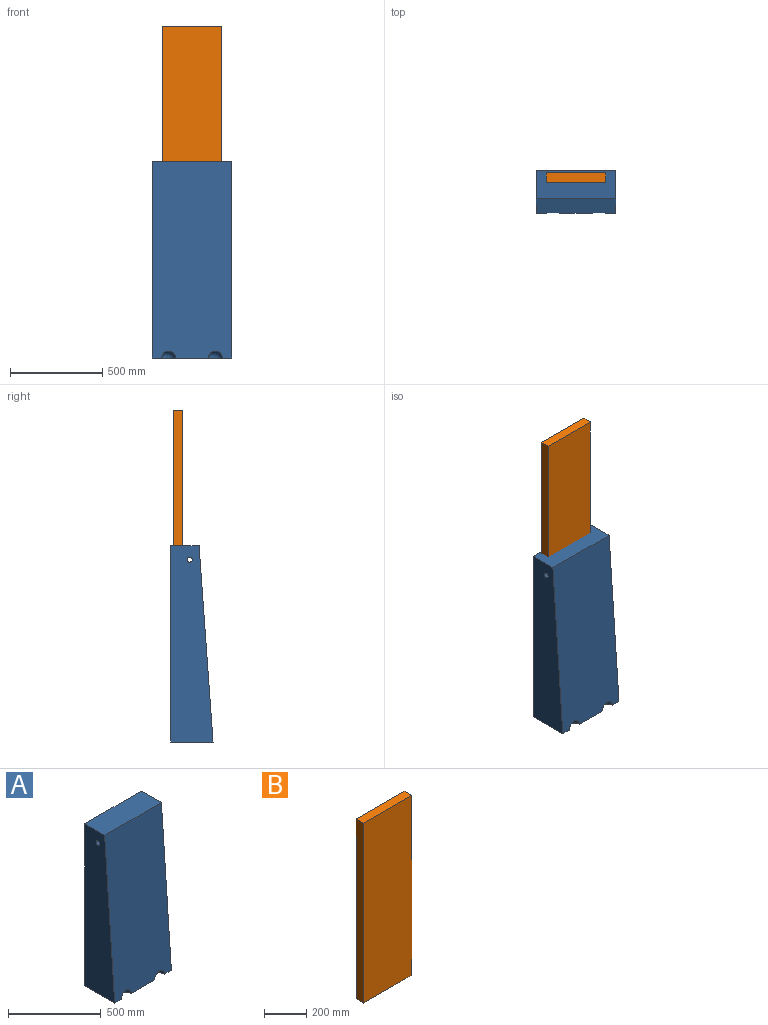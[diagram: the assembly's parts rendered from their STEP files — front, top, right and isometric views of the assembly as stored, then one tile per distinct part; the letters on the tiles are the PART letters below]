
ASSEMBLY  parts=2 mates=1
PART A: 21 faces, bbox 431.8x228.6x1066.8 mm
  f0: plane 431.8x228.6mm, normal (0,0,-1), area 93959.1mm2, adj f1,f3,f4,f5,f6,f7,f8,f10
  f1: plane 1066.8x431.8mm, normal (0,1,0), area 460644.2mm2, adj f0,f2,f4,f5
  f2: plane 431.8x152.4mm, normal (0,0,1), area 65806.3mm2, adj f1,f3,f4,f5
  f3: plane 1066.8x431.8mm, normal (0,-1,0.07), area 457257.5mm2, adj f0,f2,f4,f5,f6,f7
  f4: plane 1066.8x228.6mm, normal (1,0,0), area 202584.1mm2, adj f0,f1,f2,f3,f20
  f5: plane 1066.8x228.6mm, normal (-1,0,0), area 202584.1mm2, adj f0,f1,f2,f3,f20
  f6: sphere r=38.1mm, area 4353.3mm2, adj f0,f3
  f7: sphere r=38.1mm, area 4353.3mm2, adj f0,f3
  f8: cylinder r=3.17mm len=25.4mm, axis (0,0,-1), area 506.7mm2, adj f0,f9
  f9: plane 6.35x6.35mm, normal (0,0,-1), area 31.7mm2, adj f8
  f10: cylinder r=3.17mm len=25.4mm, axis (0,0,-1), area 506.7mm2, adj f0,f11
  f11: plane 6.35x6.35mm, normal (0,0,-1), area 31.7mm2, adj f10
  f12: cylinder r=3.17mm len=25.4mm, axis (0,0,-1), area 506.7mm2, adj f0,f13
  f13: plane 6.35x6.35mm, normal (0,0,-1), area 31.7mm2, adj f12
  f14: cylinder r=3.17mm len=25.4mm, axis (0,0,-1), area 506.7mm2, adj f0,f15
  f15: plane 6.35x6.35mm, normal (0,0,-1), area 31.7mm2, adj f14
  f16: cylinder r=3.17mm len=25.4mm, axis (0,0,-1), area 506.7mm2, adj f0,f17
  f17: plane 6.35x6.35mm, normal (0,0,-1), area 31.7mm2, adj f16
  f18: cylinder r=3.17mm len=25.4mm, axis (0,0,-1), area 506.7mm2, adj f0,f19
  f19: plane 6.35x6.35mm, normal (0,0,-1), area 31.7mm2, adj f18
  f20: cylinder r=14.29mm len=431.8mm, axis (1,0,0), area 38763.1mm2, adj f4,f5
PART B: 6 faces, bbox 323.9x50.8x1041.4 mm
  f0: plane 323.85x50.8mm, normal (0,0,1), area 16451.6mm2, adj f1,f3,f4,f5
  f1: plane 1041.4x323.85mm, normal (0,-1,0), area 337257.4mm2, adj f0,f2,f4,f5
  f2: plane 323.85x50.8mm, normal (0,0,-1), area 16451.6mm2, adj f1,f3,f4,f5
  f3: plane 1041.4x323.85mm, normal (0,1,0), area 337257.4mm2, adj f0,f2,f4,f5
  f4: plane 1041.4x50.8mm, normal (1,0,0), area 52903.1mm2, adj f0,f1,f2,f3
  f5: plane 1041.4x50.8mm, normal (-1,0,0), area 52903.1mm2, adj f0,f1,f2,f3
PLACE A at identity fixed
PLACE B t=(0,184.96,250.4)mm
MATE slider A.f2 <-> B.f0  axis (0,0,1) through (0,0,1066.8)mm
